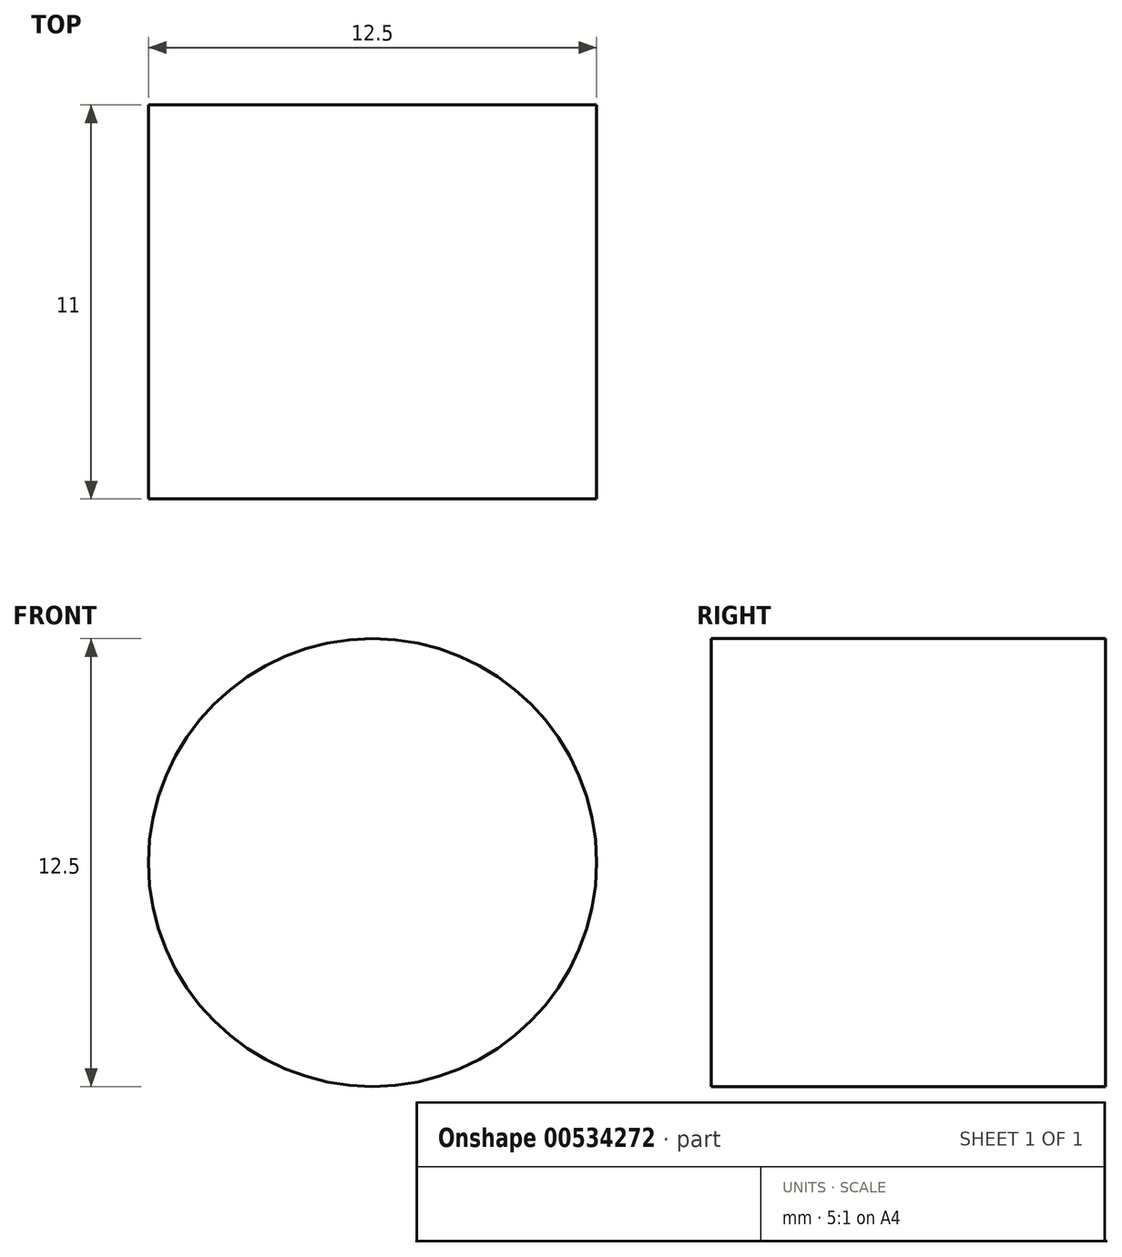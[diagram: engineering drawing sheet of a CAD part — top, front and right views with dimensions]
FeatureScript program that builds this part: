
annotation { "Feature Type Name" : "Feature", "Feature Type Description" : "" }
export const myFeature = defineFeature(function(context is Context, id is Id, definition is map)
    precondition{}
    {
        {
            var Q0;
            Q0=qCreatedBy(makeId("Front.planeOp"),FACE);
            var sketch = newSketch(context, id + "F0", { "sketchPlane" : qUnion([Q0])});
            skCircle(sketch, "E0", {"center": v(0, 0) * mm, "radius": 6.25 * mm});
            skSolve(sketch);
        }
        {
            var Q0;
            Q0=makeQuery(id+"F0.imprint","IMPRINT",FACE,{"disambiguationData":[TD([[makeQuery(id+"F0.imprint","IMPRINT",EDGE,{"derivedFrom":sQuery(id+"F0.wireOp",EDGE,"E0")}),1.0]])]});
            var Q1;
            Q1=sQuery(id+"F0.wireOp",EDGE,"E0");
            extrude(context, id + "F1", {"entities" : qUnion([Q0]), "surfaceEntities" : qUnion([Q1]), "depth" : 11 * mm, "offsetDistance" : 25 * mm});
        }
    });
